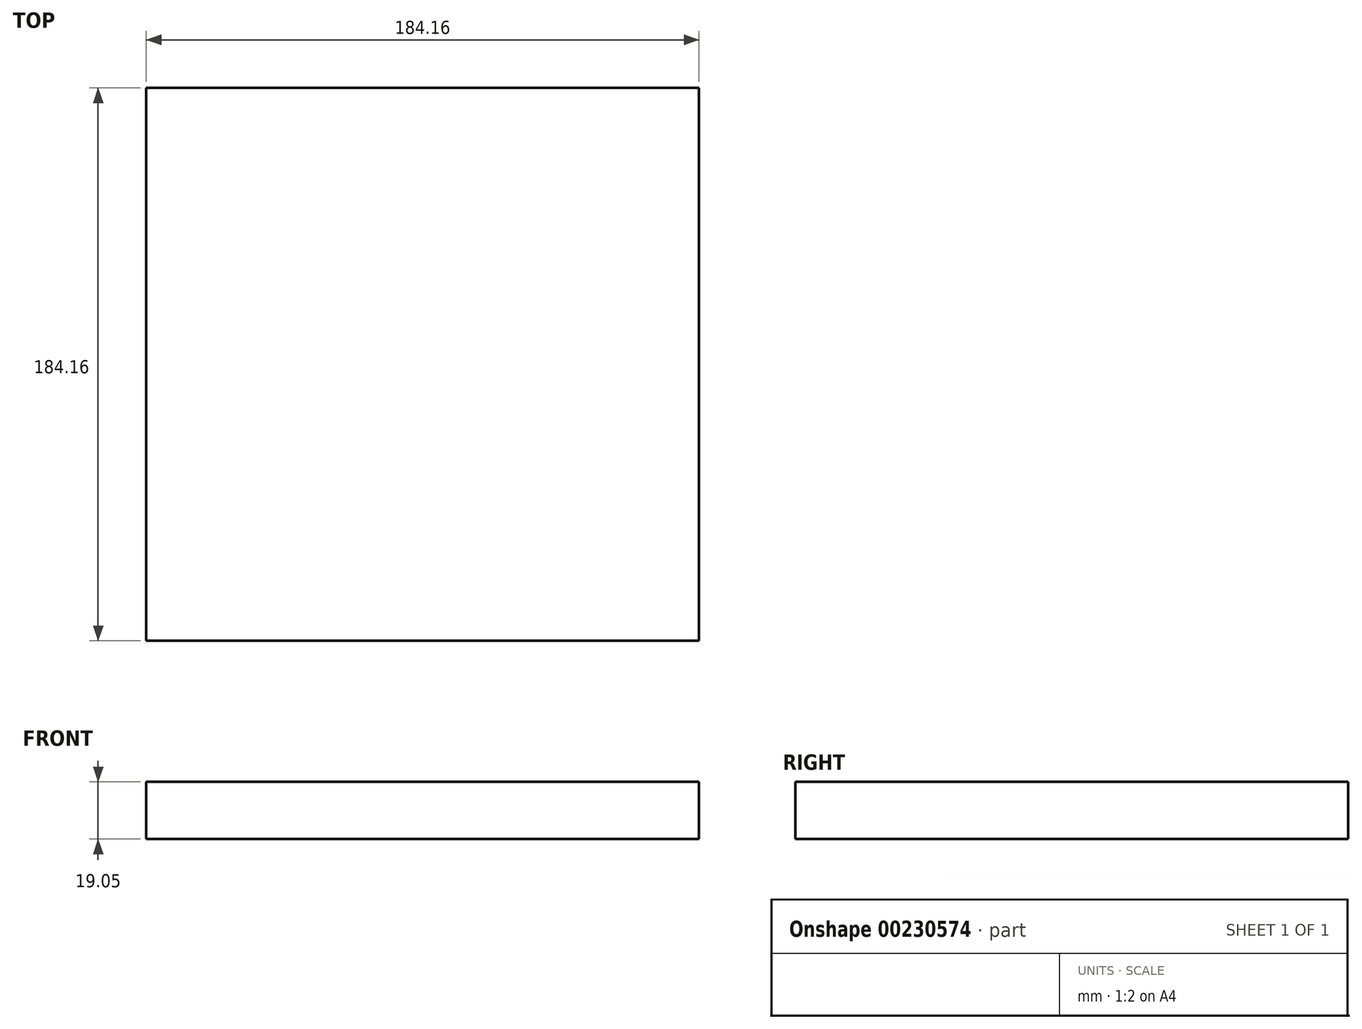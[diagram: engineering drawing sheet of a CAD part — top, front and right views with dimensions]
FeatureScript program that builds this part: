
annotation { "Feature Type Name" : "Feature", "Feature Type Description" : "" }
export const myFeature = defineFeature(function(context is Context, id is Id, definition is map)
    precondition{}
    {
        {
            var Q0;
            Q0=qCreatedBy(makeId("Top.planeOp"),FACE);
            var sketch = newSketch(context, id + "F0", { "sketchPlane" : qUnion([Q0])});
            skLineSegment(sketch, "E0.bottom", {"start": v(92.08, 92.08) * mm, "end": v(-92.07, 92.08) * mm});
            skLineSegment(sketch, "E0.top", {"start": v(92.07, -92.08) * mm, "end": v(-92.07, -92.08) * mm});
            skLineSegment(sketch, "E0.left", {"start": v(92.08, 92.08) * mm, "end": v(92.07, -92.07) * mm});
            skLineSegment(sketch, "E0.right", {"start": v(-92.07, 92.08) * mm, "end": v(-92.08, -92.07) * mm});
            skPoint(sketch, "E0.middle", {"position": v(0, 0) * mm});
            skSolve(sketch);
        }
        {
            var Q0;
            Q0 = qSketchRegion(id + "F0", true);
            extrude(context, id + "F1", {"entities" : qUnion([Q0]), "depth" : 19.05 * mm});
        }
    });
